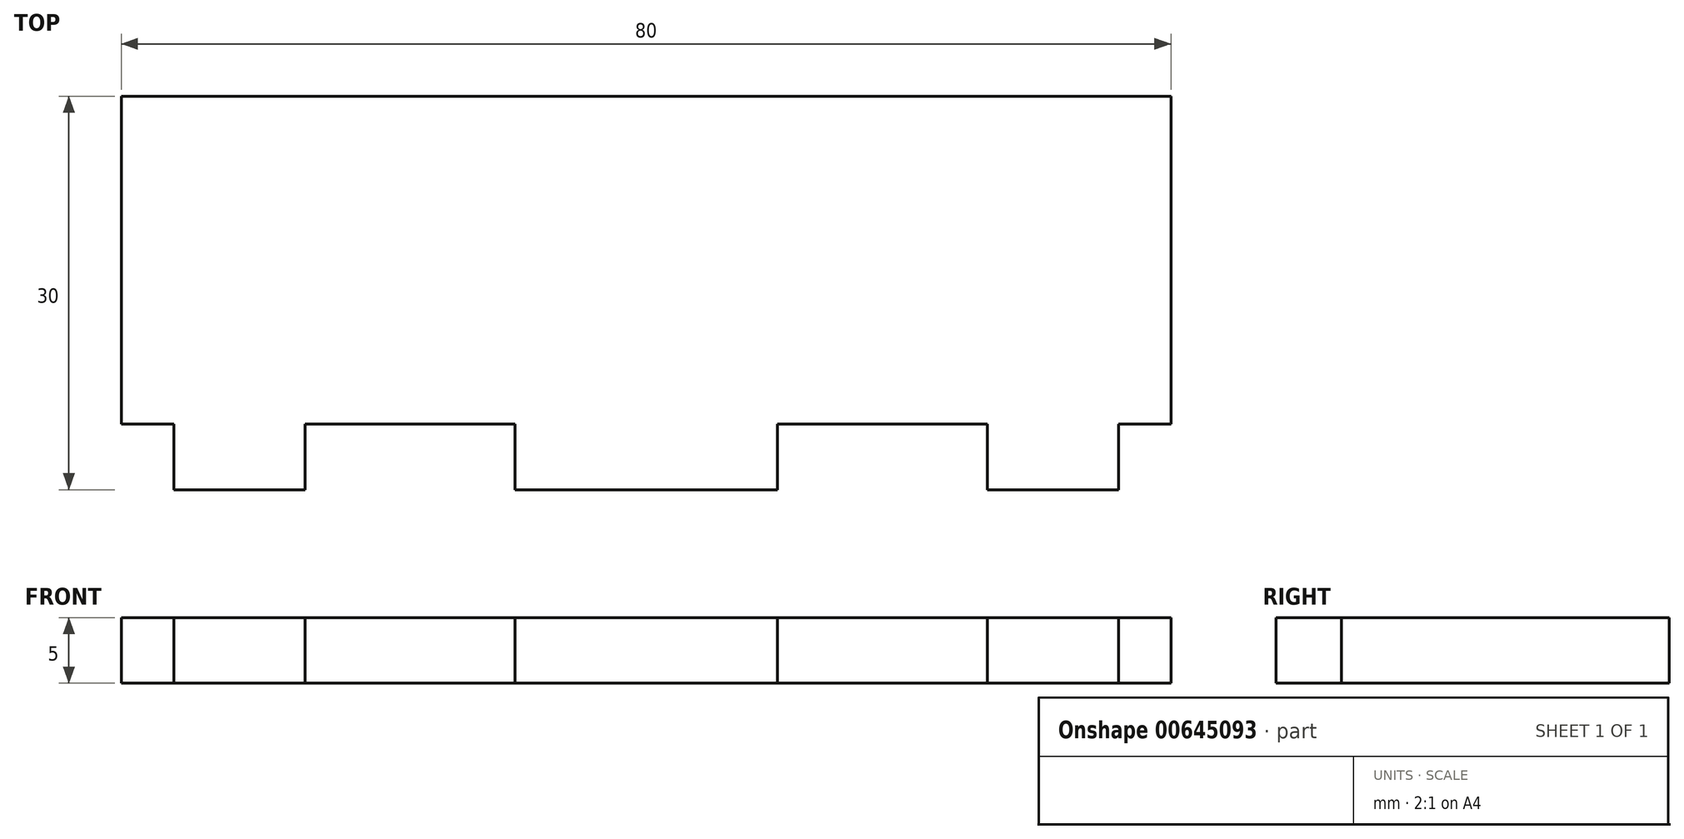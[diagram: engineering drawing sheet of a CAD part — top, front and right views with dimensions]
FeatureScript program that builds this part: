
annotation { "Feature Type Name" : "Feature", "Feature Type Description" : "" }
export const myFeature = defineFeature(function(context is Context, id is Id, definition is map)
    precondition{}
    {
        {
            var Q0;
            Q0=qCreatedBy(makeId("Top.planeOp"),FACE);
            var sketch = newSketch(context, id + "F0", { "sketchPlane" : qUnion([Q0])});
            skLineSegment(sketch, "E0.bottom", {"start": v(40, -12.5) * mm, "end": v(36, -12.5) * mm});
            skLineSegment(sketch, "E0.top", {"start": v(40, 12.5) * mm, "end": v(-40, 12.5) * mm});
            skLineSegment(sketch, "E0.left", {"start": v(40, -12.5) * mm, "end": v(40, 12.5) * mm});
            skLineSegment(sketch, "E0.right", {"start": v(-40, -12.5) * mm, "end": v(-40, 12.5) * mm});
            skPoint(sketch, "E0.middle", {"position": v(0, 0) * mm});
            skLineSegment(sketch, "E1.bottom", {"start": v(-40, -12.5) * mm, "end": v(-36, -12.5) * mm});
            skLineSegment(sketch, "E1.top", {"start": v(-36, -17.5) * mm, "end": v(-26, -17.5) * mm});
            skLineSegment(sketch, "E2", {"start": v(-36, -12.5) * mm, "end": v(-36, -17.5) * mm});
            skLineSegment(sketch, "E3", {"start": v(-26, -12.5) * mm, "end": v(-26, -17.5) * mm});
            skLineSegment(sketch, "E4", {"start": v(-10, -12.5) * mm, "end": v(-10, -17.5) * mm});
            skLineSegment(sketch, "E5", {"start": v(10, -12.5) * mm, "end": v(10, -17.5) * mm});
            skLineSegment(sketch, "E6", {"start": v(36, -12.5) * mm, "end": v(36, -17.5) * mm});
            skLineSegment(sketch, "E7", {"start": v(26, -12.5) * mm, "end": v(26, -17.5) * mm});
            skLineSegment(sketch, "E8.trimOffspring", {"start": v(-10, -17.5) * mm, "end": v(10, -17.5) * mm});
            skLineSegment(sketch, "E9.trimOffspring", {"start": v(26, -17.5) * mm, "end": v(36, -17.5) * mm});
            skPoint(sketch, "E10.orphan", {"position": v(40, -17.5) * mm});
            skLineSegment(sketch, "E11.trimOffspring", {"start": v(-26, -12.5) * mm, "end": v(-10, -12.5) * mm});
            skLineSegment(sketch, "E12.trimOffspring", {"start": v(-10, -12.5) * mm, "end": v(-26, -12.5) * mm});
            skLineSegment(sketch, "E13.trimOffspring", {"start": v(26, -12.5) * mm, "end": v(10, -12.5) * mm});
            skLineSegment(sketch, "E14.trimOffspring", {"start": v(36, -12.5) * mm, "end": v(40.72, -12.5) * mm});
            skLineSegment(sketch, "E15.trimOffspring", {"start": v(10, -12.5) * mm, "end": v(26, -12.5) * mm});
            skLineSegment(sketch, "E16.trimOffspring", {"start": v(-36, -12.5) * mm, "end": v(-40, -12.5) * mm});
            skSolve(sketch);
        }
        {
            var Q0;
            Q0 = qSketchRegion(id + "F0", true);
            extrude(context, id + "F1", {"entities" : qUnion([Q0]), "depth" : 5 * mm, "offsetDistance" : 25 * mm});
        }
    });
